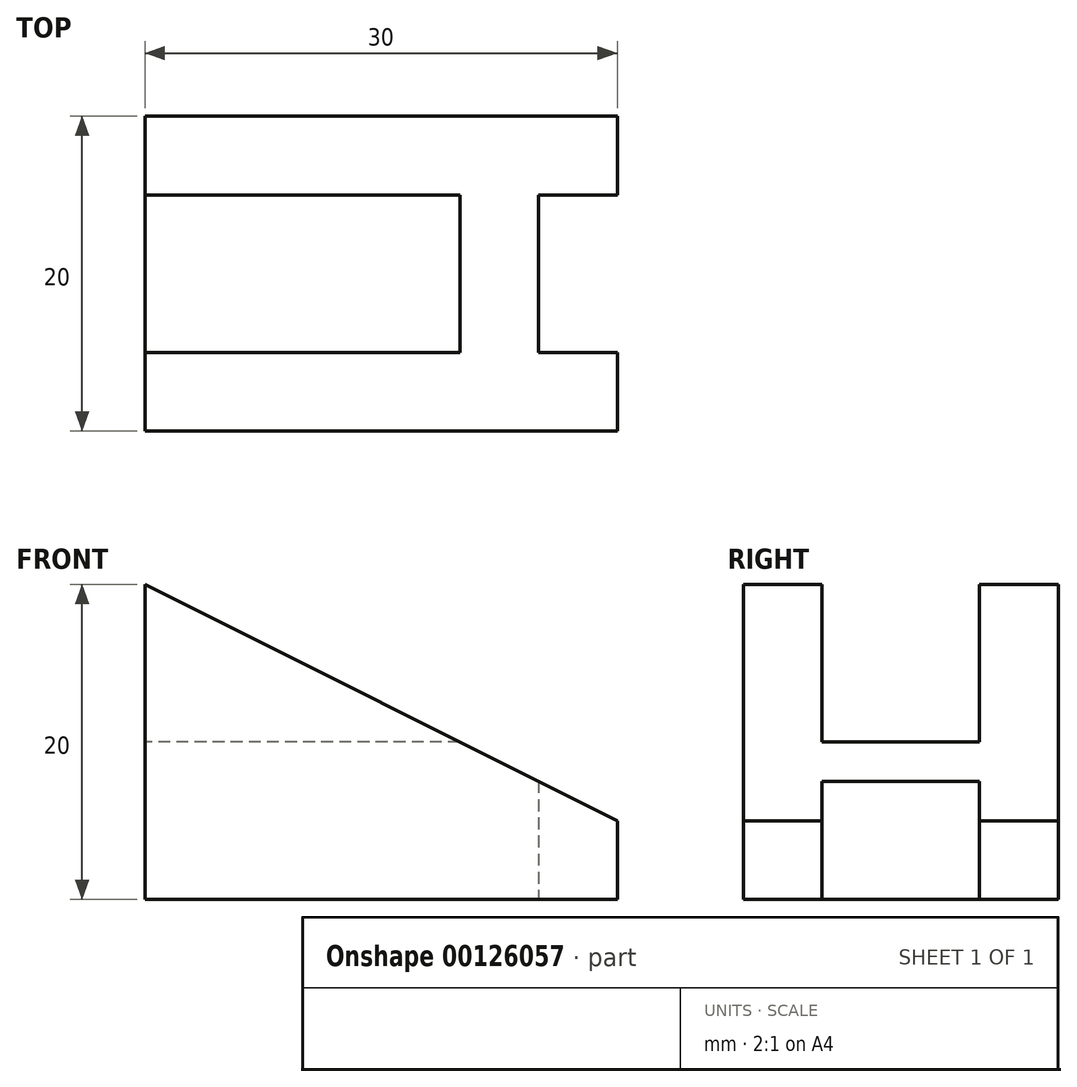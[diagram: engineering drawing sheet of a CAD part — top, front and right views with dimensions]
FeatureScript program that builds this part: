
annotation { "Feature Type Name" : "Feature", "Feature Type Description" : "" }
export const myFeature = defineFeature(function(context is Context, id is Id, definition is map)
    precondition{}
    {
        {
            var Q0;
            Q0=qCreatedBy(makeId("Front.planeOp"),FACE);
            var sketch = newSketch(context, id + "F0", { "sketchPlane" : qUnion([Q0])});
            skLineSegment(sketch, "E0", {"start": v(0, 0) * mm, "end": v(-30, 0) * mm});
            skLineSegment(sketch, "E1", {"start": v(-30, 0) * mm, "end": v(-30, 20) * mm});
            skLineSegment(sketch, "E2", {"start": v(0, 0) * mm, "end": v(0, 5) * mm});
            skLineSegment(sketch, "E3", {"start": v(0, 5) * mm, "end": v(-30, 20) * mm});
            skSolve(sketch);
        }
        {
            var Q0;
            Q0 = qSketchRegion(id + "F0", true);
            extrude(context, id + "F1", {"entities" : qUnion([Q0]), "oppositeDirection" : true, "depth" : 20 * mm});
        }
        {
            var Q0;
            Q0=makeQuery(id+"F1.opExtrude","SWEPT_FACE",FACE,{"disambiguationData":[OSD([sQuery(id+"F0.wireOp",EDGE,"E1")])]});
            var sketch = newSketch(context, id + "F2", { "sketchPlane" : qUnion([Q0])});
            skLineSegment(sketch, "E4", {"start": v(-15, 20) * mm, "end": v(-15, 10) * mm});
            skLineSegment(sketch, "E5", {"start": v(-15, 10) * mm, "end": v(-5, 10) * mm});
            skLineSegment(sketch, "E6", {"start": v(-5, 10) * mm, "end": v(-5, 20) * mm});
            skLineSegment(sketch, "E7", {"start": v(-5, 20) * mm, "end": v(-15, 20) * mm});
            skSolve(sketch);
        }
        {
            var Q0;
            Q0 = qSketchRegion(id + "F2", true);
            extrude(context, id + "F3", {"entities" : qUnion([Q0]), "operationType" : NewBodyOperationType.REMOVE, "endBound" : BoundingType.THROUGH_ALL, "oppositeDirection" : true, "depth" : 25 * mm});
        }
        {
            var Q0;
            Q0=makeQuery(id+"F1.opExtrude","SWEPT_FACE",FACE,{"disambiguationData":[OSD([sQuery(id+"F0.wireOp",EDGE,"E0")])]});
            var sketch = newSketch(context, id + "F4", { "sketchPlane" : qUnion([Q0])});
            skLineSegment(sketch, "E8", {"start": v(0, -5) * mm, "end": v(-5, -5) * mm});
            skLineSegment(sketch, "E9", {"start": v(-5, -5) * mm, "end": v(-5, -15) * mm});
            skLineSegment(sketch, "E10", {"start": v(-5, -15) * mm, "end": v(0, -15) * mm});
            skLineSegment(sketch, "E11", {"start": v(0, -15) * mm, "end": v(0, -5) * mm});
            skSolve(sketch);
        }
        {
            var Q0;
            Q0 = qSketchRegion(id + "F4", true);
            extrude(context, id + "F5", {"entities" : qUnion([Q0]), "operationType" : NewBodyOperationType.REMOVE, "endBound" : BoundingType.THROUGH_ALL, "oppositeDirection" : true, "depth" : 25 * mm});
        }
    });
